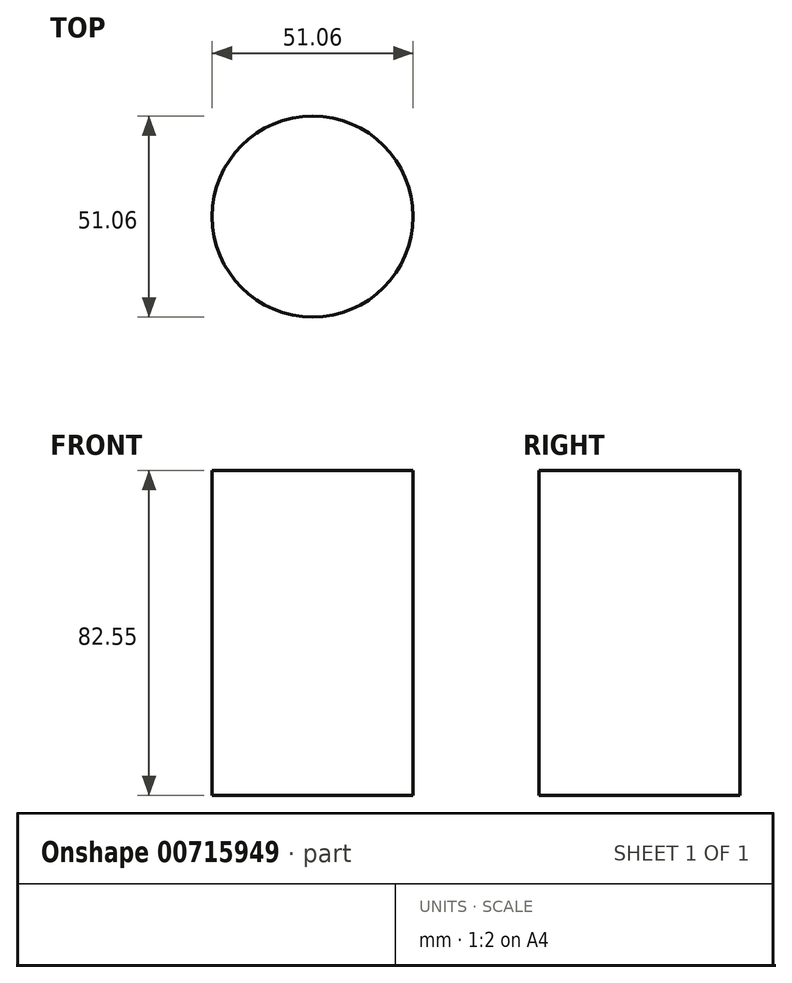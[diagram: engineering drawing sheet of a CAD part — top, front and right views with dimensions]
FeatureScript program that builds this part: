
annotation { "Feature Type Name" : "Feature", "Feature Type Description" : "" }
export const myFeature = defineFeature(function(context is Context, id is Id, definition is map)
    precondition{}
    {
        {
            var Q0;
            Q0=qCreatedBy(makeId("Top.planeOp"),FACE);
            var sketch = newSketch(context, id + "F0", { "sketchPlane" : qUnion([Q0])});
            skCircle(sketch, "E0", {"center": v(0, 0) * mm, "radius": 25.53 * mm});
            skSolve(sketch);
        }
        {
            var Q0;
            Q0=makeQuery(id+"F0.imprint","IMPRINT",FACE,{"disambiguationData":[TD([[makeQuery(id+"F0.imprint","IMPRINT",EDGE,{"derivedFrom":sQuery(id+"F0.wireOp",EDGE,"E0")}),1.0]])]});
            extrude(context, id + "F1", {"entities" : qUnion([Q0]), "depth" : 82.55 * mm, "offsetDistance" : 25.4 * mm});
        }
    });
